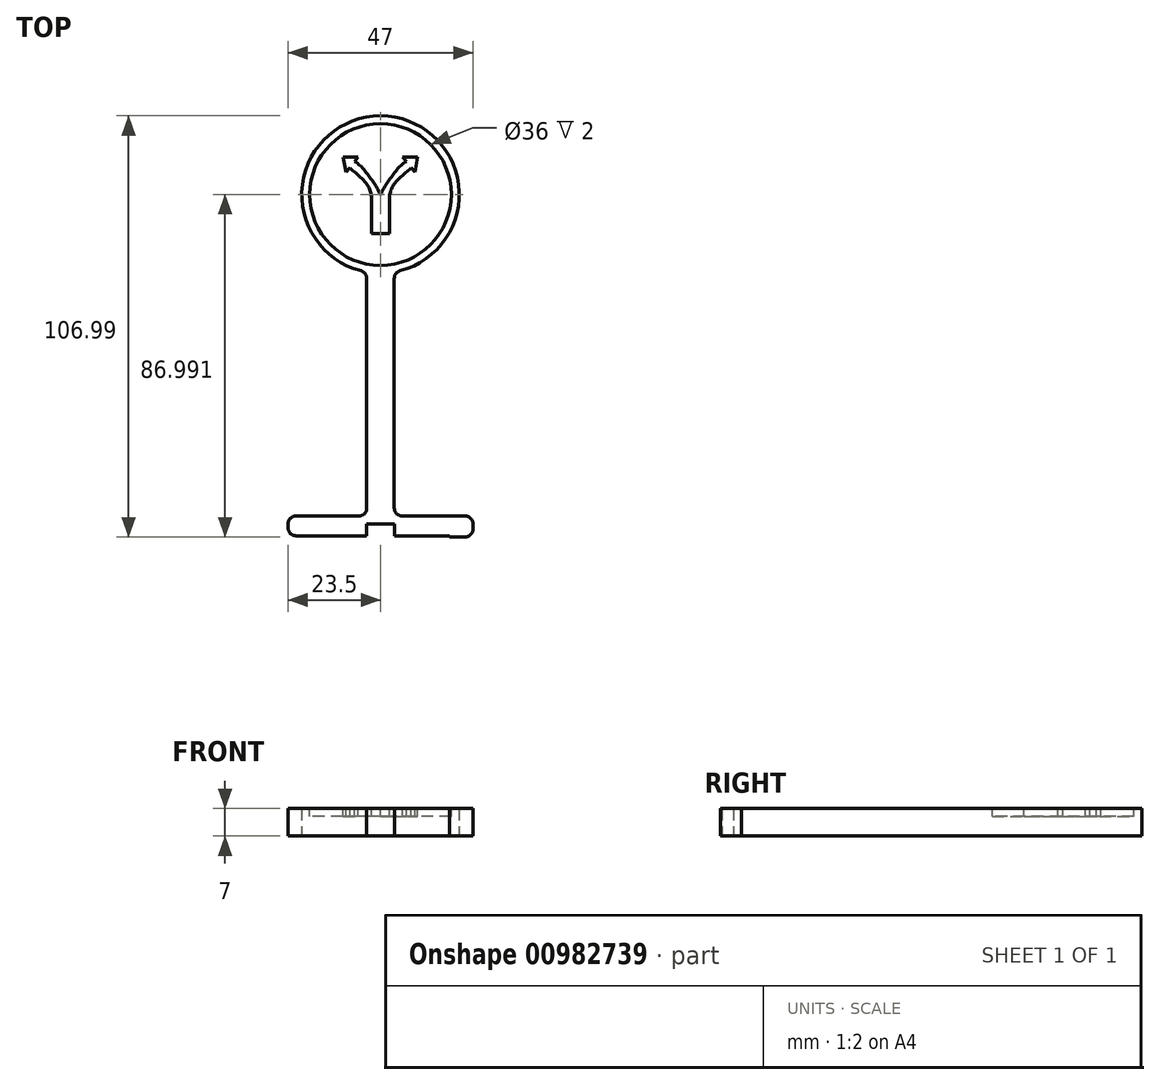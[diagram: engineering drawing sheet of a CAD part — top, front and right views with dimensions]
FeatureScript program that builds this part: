
annotation { "Feature Type Name" : "Feature", "Feature Type Description" : "" }
export const myFeature = defineFeature(function(context is Context, id is Id, definition is map)
    precondition{}
    {
        {
            var Q0;
            Q0=qCreatedBy(makeId("Top.planeOp"),FACE);
            var sketch = newSketch(context, id + "F0", { "sketchPlane" : qUnion([Q0])});
            skLineSegment(sketch, "E0", {"start": v(-3.5, -3) * mm, "end": v(-3.5, -65) * mm});
            skLineSegment(sketch, "E1", {"start": v(-3.5, -65) * mm, "end": v(-23.5, -65) * mm});
            skLineSegment(sketch, "E2", {"start": v(-23.5, -65) * mm, "end": v(-23.5, -70) * mm});
            skLineSegment(sketch, "E3", {"start": v(-23.5, -70) * mm, "end": v(23.5, -70) * mm});
            skLineSegment(sketch, "E4", {"start": v(23.5, -70) * mm, "end": v(23.5, -65) * mm});
            skLineSegment(sketch, "E5", {"start": v(23.5, -65) * mm, "end": v(3.5, -65) * mm});
            skLineSegment(sketch, "E6", {"start": v(3.5, -65) * mm, "end": v(3.5, -3) * mm});
            skLineSegment(sketch, "E7.bottom", {"start": v(3.6, -70) * mm, "end": v(-3.6, -70) * mm});
            skLineSegment(sketch, "E7.top", {"start": v(3.6, -67) * mm, "end": v(-3.6, -67) * mm});
            skLineSegment(sketch, "E7.left", {"start": v(3.6, -70) * mm, "end": v(3.6, -67) * mm});
            skLineSegment(sketch, "E7.right", {"start": v(-3.6, -70) * mm, "end": v(-3.6, -67) * mm});
            skPoint(sketch, "E7.middle", {"position": v(0, -68.5) * mm});
            skCircle(sketch, "E8", {"center": v(0, 16.7) * mm, "radius": 20 * mm});
            skLineSegment(sketch, "E9.bottom", {"start": v(-23.5, -70) * mm, "end": v(-17.5, -70) * mm});
            skLineSegment(sketch, "E9.top", {"start": v(-23.5, -70.3) * mm, "end": v(-17.5, -70.3) * mm});
            skLineSegment(sketch, "E9.left", {"start": v(-23.5, -70) * mm, "end": v(-23.5, -70.3) * mm});
            skLineSegment(sketch, "E9.right", {"start": v(-17.5, -70) * mm, "end": v(-17.5, -70.3) * mm});
            skLineSegment(sketch, "E10.MirrorCS", {"start": v(23.5, -70.3) * mm, "end": v(17.5, -70.3) * mm});
            skLineSegment(sketch, "E11.MirrorCS", {"start": v(23.5, -70) * mm, "end": v(17.5, -70) * mm});
            skLineSegment(sketch, "E12.MirrorCS", {"start": v(23.5, -70) * mm, "end": v(23.5, -70.3) * mm});
            skLineSegment(sketch, "E13.MirrorCS", {"start": v(17.5, -70) * mm, "end": v(17.5, -70.3) * mm});
            skSolve(sketch);
        }
        {
            var Q0;
            Q0=makeQuery(id+"F0.imprint","IMPRINT",FACE,{"disambiguationData":[TD([[makeQuery(id+"F0.imprint","IMPRINT",EDGE,{"derivedFrom":sQuery(id+"F0.wireOp",EDGE,"0U4RxweM-u2bA-2Qqt-OOBg-x1ftkZs6jUrD")}),1.0]])]});
            var Q1;
            {var subQ0=sQuery(id+"F0.wireOp",EDGE,"im0v1Rov-prSM-cwdN-f0IW-ScqFdnQkXUSi");Q1=makeQuery(id+"F0.imprint","IMPRINT",FACE,{"disambiguationData":[TD([[makeQuery(id+"F0.imprint","IMPRINT",EDGE,{"derivedFrom":subQ0}),1.0]])]});}
            var Q2;
            {var subQ7=sQuery(id+"F0.wireOp",EDGE,"E0");Q2=makeQuery(id+"F0.imprint","IMPRINT",FACE,{"disambiguationData":[TD([[makeQuery(id+"F0.imprint","IMPRINT",EDGE,{"derivedFrom":subQ7}),1.0]])]});}
            var Q3;
            {var subQ0=sQuery(id+"F0.wireOp",EDGE,"E8");var subQ1=makeQuery(id+"F0.imprint","INTERSECT",VERTEX,{"derivedFrom":[sQuery(id+"F0.wireOp",EDGE,"E0"),subQ0]});Q3=makeQuery(id+"F0.imprint","IMPRINT",FACE,{"disambiguationData":[TD([[makeQuery(id+"F0.imprint","IMPRINT",EDGE,{"disambiguationData":[TD([[subQ1,-1.0]])],"derivedFrom":subQ0}),1.0]])]});}
            var Q4;
            Q4=makeQuery(id+"F0.imprint","IMPRINT",FACE,{"disambiguationData":[TD([[makeQuery(id+"F0.imprint","IMPRINT",EDGE,{"derivedFrom":sQuery(id+"F0.wireOp",EDGE,"E9.bottom")}),-1.0]])]});
            var Q5;
            Q5=makeQuery(id+"F0.imprint","IMPRINT",FACE,{"disambiguationData":[TD([[makeQuery(id+"F0.imprint","IMPRINT",EDGE,{"derivedFrom":sQuery(id+"F0.wireOp",EDGE,"E10.MirrorCS")}),-1.0]])]});
            extrude(context, id + "F1", {"entities" : qUnion([Q0, Q1, Q2, Q3, Q4, Q5]), "depth" : 7 * mm, "offsetDistance" : 25 * mm});
        }
        {
            var Q0;
            Q0=makeQuery(id+"F1.opExtrude","CAP_FACE",FACE,{"disambiguationData":[OSD([sQuery(id+"F0.wireOp",EDGE,"E0"),sQuery(id+"F0.wireOp",EDGE,"E1"),sQuery(id+"F0.wireOp",EDGE,"E2"),sQuery(id+"F0.wireOp",EDGE,"E3"),sQuery(id+"F0.wireOp",EDGE,"E4"),sQuery(id+"F0.wireOp",EDGE,"E5"),sQuery(id+"F0.wireOp",EDGE,"E6"),sQuery(id+"F0.wireOp",EDGE,"E7.top"),sQuery(id+"F0.wireOp",EDGE,"E7.left"),sQuery(id+"F0.wireOp",EDGE,"E7.right"),sQuery(id+"F0.wireOp",EDGE,"E8")])],"isStart":false});
            var sketch = newSketch(context, id + "F2", { "sketchPlane" : qUnion([Q0])});
            skCircle(sketch, "E14", {"center": v(0, 16.7) * mm, "radius": 18 * mm});
            skLineSegment(sketch, "E15", {"start": v(-2.26, 6.74) * mm, "end": v(0, 6.74) * mm});
            skLineSegment(sketch, "E16", {"start": v(-2.26, 6.74) * mm, "end": v(-2.26, 15.38) * mm});
            skFitSpline(sketch, "E17", {"points": [v(-2.26, 15.38) * mm, v(-3.57, 19.52) * mm, v(-7.77, 23.48) * mm], "startDerivative": vector(-0.43, 9.4) * mm, "endDerivative": vector(-3.37, 3.82) * mm});
            skLineSegment(sketch, "E18", {"start": v(-7.77, 23.48) * mm, "end": v(-8.75, 22.35) * mm});
            skLineSegment(sketch, "E19", {"start": v(-8.75, 22.35) * mm, "end": v(-9.46, 26.26) * mm});
            skLineSegment(sketch, "E20", {"start": v(-9.46, 26.26) * mm, "end": v(-5.64, 26.26) * mm});
            skLineSegment(sketch, "E21", {"start": v(-5.64, 26.26) * mm, "end": v(-6.62, 25.12) * mm});
            skLineSegment(sketch, "E22", {"start": v(-7.23, 24.33) * mm, "end": v(-9.96, 26.7) * mm, "construction": true});
            skFitSpline(sketch, "E23", {"points": [v(0, 16.7) * mm, v(-2.94, 21.4) * mm, v(-6.62, 25.12) * mm], "startDerivative": vector(-5.01, 10.03) * mm, "endDerivative": vector(-9, 4.8) * mm});
            skLineSegment(sketch, "E24.MirrorCS", {"start": v(7.77, 23.48) * mm, "end": v(8.75, 22.35) * mm});
            skLineSegment(sketch, "E25.MirrorCS", {"start": v(7.23, 24.33) * mm, "end": v(9.96, 26.7) * mm, "construction": true});
            skLineSegment(sketch, "E26.MirrorCS", {"start": v(9.46, 26.26) * mm, "end": v(5.64, 26.26) * mm});
            skFitSpline(sketch, "E27.MirrorCS", {"points": [v(2.26, 15.38) * mm, v(3.57, 19.52) * mm, v(7.77, 23.48) * mm], "startDerivative": vector(0.43, 9.4) * mm, "endDerivative": vector(3.37, 3.82) * mm});
            skLineSegment(sketch, "E28.MirrorCS", {"start": v(2.26, 6.74) * mm, "end": v(2.26, 15.38) * mm});
            skLineSegment(sketch, "E29.MirrorCS", {"start": v(5.64, 26.26) * mm, "end": v(6.62, 25.12) * mm});
            skFitSpline(sketch, "E30.MirrorCS", {"points": [v(0, 16.7) * mm, v(2.94, 21.4) * mm, v(6.62, 25.12) * mm], "startDerivative": vector(5.01, 10.03) * mm, "endDerivative": vector(9, 4.8) * mm});
            skLineSegment(sketch, "E31.MirrorCS", {"start": v(2.26, 6.74) * mm, "end": v(0, 6.74) * mm});
            skLineSegment(sketch, "E32.MirrorCS", {"start": v(8.75, 22.35) * mm, "end": v(9.46, 26.26) * mm});
            skSolve(sketch);
        }
        {
            var Q0;
            Q0=makeQuery(id+"F2.imprint","IMPRINT",FACE,{"disambiguationData":[TD([[makeQuery(id+"F2.imprint","IMPRINT",EDGE,{"derivedFrom":sQuery(id+"F2.wireOp",EDGE,"E14")}),1.0]])]});
            extrude(context, id + "F3", {"entities" : qUnion([Q0]), "operationType" : NewBodyOperationType.REMOVE, "oppositeDirection" : true, "depth" : 2 * mm, "offsetDistance" : 25 * mm});
        }
        {
            var Q0;
            Q0=makeQuery(id+"F1.opExtrude","SWEPT_EDGE",EDGE,{"disambiguationData":[OSD([sQuery(id+"F0.wireOp",EDGE,"E0"),sQuery(id+"F0.wireOp",EDGE,"E8")])]});
            var Q1;
            Q1=makeQuery(id+"F1.opExtrude","SWEPT_EDGE",EDGE,{"disambiguationData":[OSD([sQuery(id+"F0.wireOp",EDGE,"E6"),sQuery(id+"F0.wireOp",EDGE,"E8")])]});
            var Q2;
            Q2=makeQuery(id+"F1.opExtrude","SWEPT_EDGE",EDGE,{"disambiguationData":[OSD([sQuery(id+"F0.wireOp",EDGE,"E4"),sQuery(id+"F0.wireOp",EDGE,"E5")])]});
            var Q3;
            Q3=makeQuery(id+"F1.opExtrude","SWEPT_EDGE",EDGE,{"disambiguationData":[OSD([sQuery(id+"F0.wireOp",EDGE,"E1"),sQuery(id+"F0.wireOp",EDGE,"E2")])]});
            var Q4;
            Q4=makeQuery(id+"F1.opExtrude","SWEPT_EDGE",EDGE,{"disambiguationData":[OSD([sQuery(id+"F0.wireOp",EDGE,"E0"),sQuery(id+"F0.wireOp",EDGE,"E1")])]});
            var Q5;
            Q5=makeQuery(id+"F1.opExtrude","SWEPT_EDGE",EDGE,{"disambiguationData":[OSD([sQuery(id+"F0.wireOp",EDGE,"E5"),sQuery(id+"F0.wireOp",EDGE,"E6")])]});
            var Q6;
            Q6=makeQuery(id+"F1.opExtrude","SWEPT_EDGE",EDGE,{"disambiguationData":[OSD([sQuery(id+"F0.wireOp",EDGE,"E9.top"),sQuery(id+"F0.wireOp",EDGE,"E9.left")])]});
            var Q7;
            Q7=makeQuery(id+"F1.opExtrude","SWEPT_EDGE",EDGE,{"disambiguationData":[OSD([sQuery(id+"F0.wireOp",EDGE,"E10.MirrorCS"),sQuery(id+"F0.wireOp",EDGE,"E12.MirrorCS")])]});
            fillet(context, id + "F4", {"entities" : qUnion([Q0, Q1, Q2, Q3, Q4, Q5, Q6, Q7]), "radius" : 2 * mm, "tangentPropagation" : true, "allowEdgeOverflow" : false});
        }
    });
